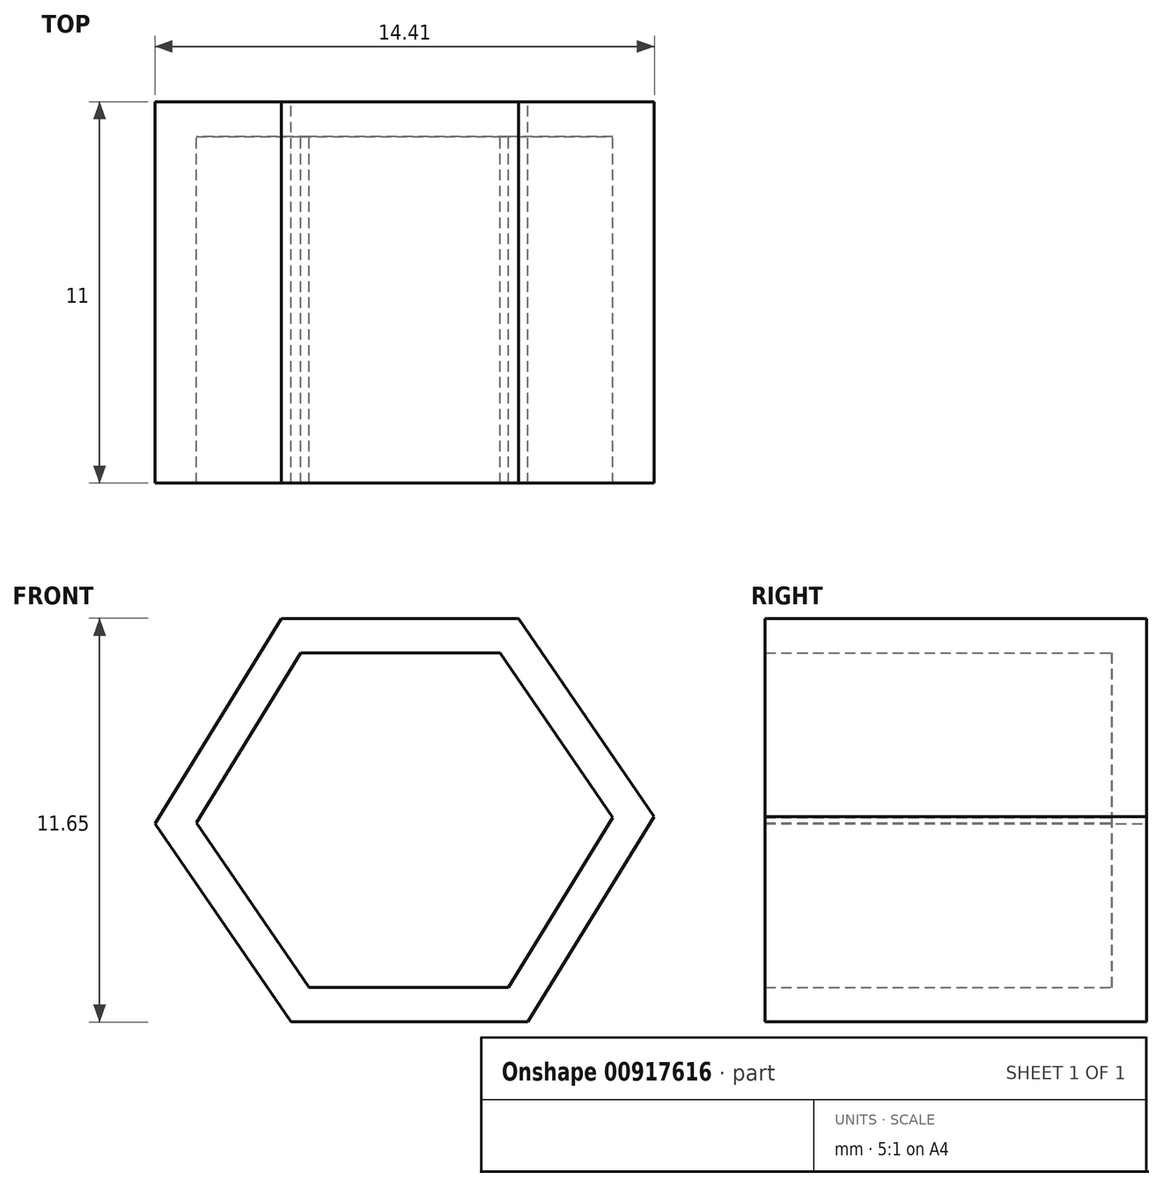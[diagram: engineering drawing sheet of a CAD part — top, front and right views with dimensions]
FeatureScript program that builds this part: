
annotation { "Feature Type Name" : "Feature", "Feature Type Description" : "" }
export const myFeature = defineFeature(function(context is Context, id is Id, definition is map)
    precondition{}
    {
        {
            var Q0;
            Q0=qCreatedBy(makeId("Front.planeOp"),FACE);
            var sketch = newSketch(context, id + "F0", { "sketchPlane" : qUnion([Q0])});
            skCircle(sketch, "E0", {"center": v(0, 0) * mm, "radius": 5 * mm});
            skLineSegment(sketch, "E1", {"start": v(-36.3, 17.57) * mm, "end": v(-33.29, 22.47) * mm});
            skLineSegment(sketch, "E2", {"start": v(-33.29, 22.47) * mm, "end": v(-27.54, 22.47) * mm});
            skLineSegment(sketch, "E3", {"start": v(-27.54, 22.47) * mm, "end": v(-24.29, 17.72) * mm});
            skLineSegment(sketch, "E4", {"start": v(-24.29, 17.72) * mm, "end": v(-27.3, 12.82) * mm});
            skLineSegment(sketch, "E5", {"start": v(-27.3, 12.82) * mm, "end": v(-33.05, 12.82) * mm});
            skLineSegment(sketch, "E6", {"start": v(-33.05, 12.82) * mm, "end": v(-36.3, 17.57) * mm});
            skSolve(sketch);
        }
        {
            var Q0;
            Q0=makeQuery(id+"F0.imprint","IMPRINT",FACE,{"disambiguationData":[TD([[makeQuery(id+"F0.imprint","IMPRINT",EDGE,{"derivedFrom":sQuery(id+"F0.wireOp",EDGE,"E1")}),-1.0]])]});
            extrude(context, id + "F1", {"entities" : qUnion([Q0]), "depth" : 10 * mm, "offsetDistance" : 25 * mm});
        }
        {
            var Q0;
            Q0=makeQuery(id+"F1.opExtrude","CAP_FACE",FACE,{"disambiguationData":[OSD([sQuery(id+"F0.wireOp",EDGE,"E1"),sQuery(id+"F0.wireOp",EDGE,"E2"),sQuery(id+"F0.wireOp",EDGE,"E3"),sQuery(id+"F0.wireOp",EDGE,"E4"),sQuery(id+"F0.wireOp",EDGE,"E5"),sQuery(id+"F0.wireOp",EDGE,"E6")])],"isStart":false});
            shell(context, id + "F2", {"entities" : qUnion([Q0]), "thickness" : 1 * mm, "oppositeDirection" : true});
        }
    });
